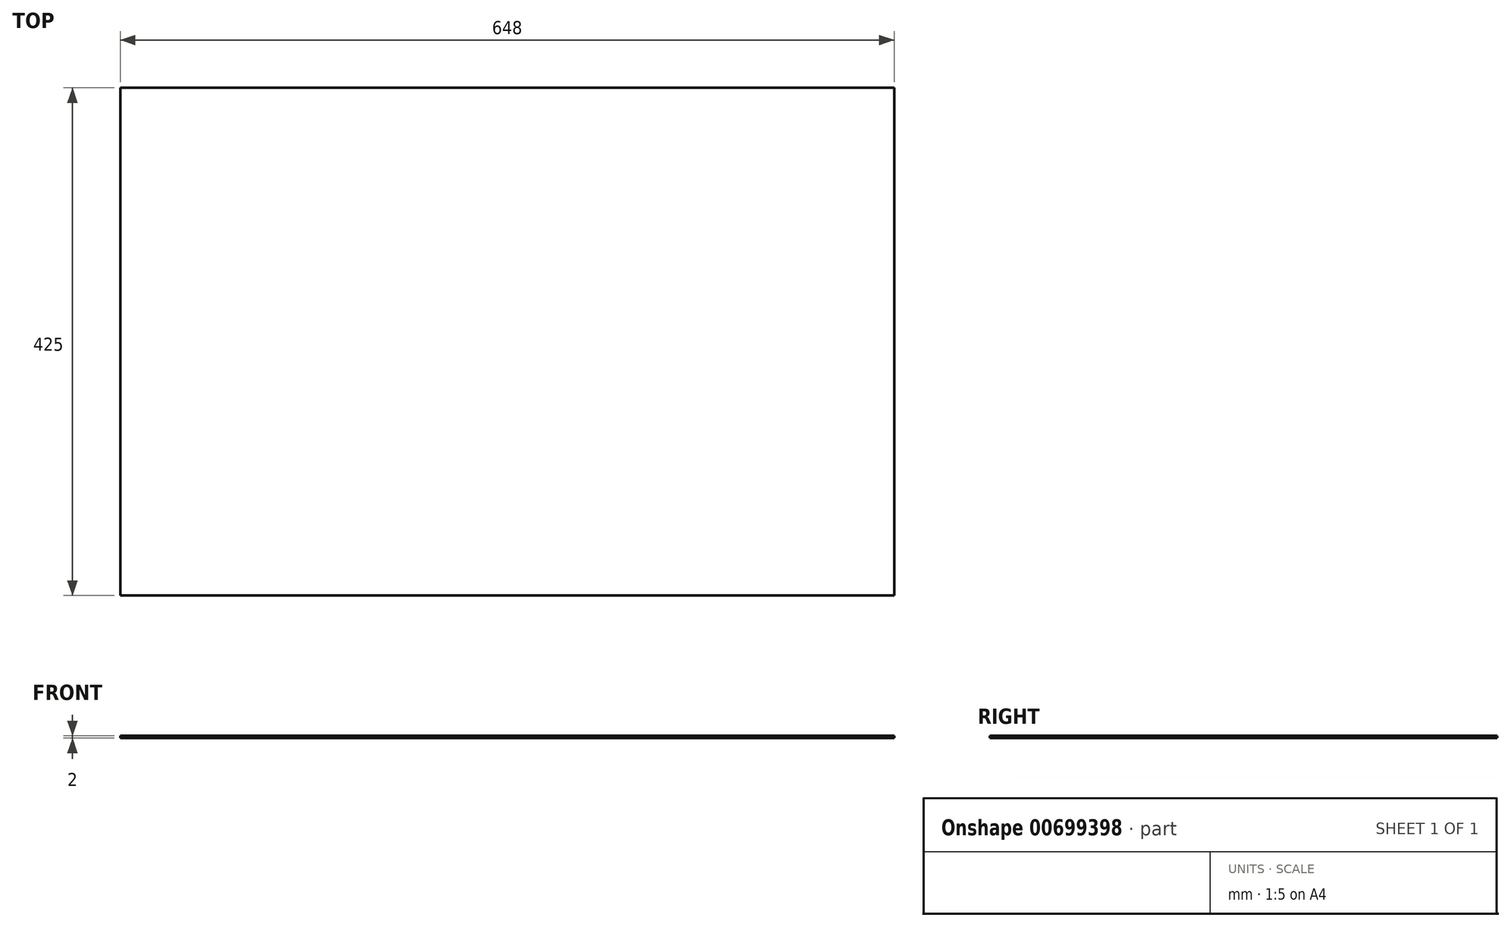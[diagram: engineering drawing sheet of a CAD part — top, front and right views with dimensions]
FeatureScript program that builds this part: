
annotation { "Feature Type Name" : "Feature", "Feature Type Description" : "" }
export const myFeature = defineFeature(function(context is Context, id is Id, definition is map)
    precondition{}
    {
        {
            var Q0;
            Q0=qCreatedBy(makeId("Top.planeOp"),FACE);
            var sketch = newSketch(context, id + "F0", { "sketchPlane" : qUnion([Q0])});
            skLineSegment(sketch, "E0.bottom", {"start": v(-295.42, 287.35) * mm, "end": v(352.58, 287.35) * mm});
            skLineSegment(sketch, "E0.top", {"start": v(-295.42, -137.65) * mm, "end": v(352.58, -137.65) * mm});
            skLineSegment(sketch, "E0.left", {"start": v(-295.42, 287.35) * mm, "end": v(-295.42, -137.65) * mm});
            skLineSegment(sketch, "E0.right", {"start": v(352.58, 287.35) * mm, "end": v(352.58, -137.65) * mm});
            skSolve(sketch);
        }
        {
            var Q0;
            Q0=makeQuery(id+"F0.imprint","IMPRINT",FACE,{"disambiguationData":[TD([[makeQuery(id+"F0.imprint","IMPRINT",EDGE,{"derivedFrom":sQuery(id+"F0.wireOp",EDGE,"E0.bottom")}),-1.0]])]});
            extrude(context, id + "F1", {"entities" : qUnion([Q0]), "depth" : 2 * mm, "offsetDistance" : 25 * mm});
        }
    });
